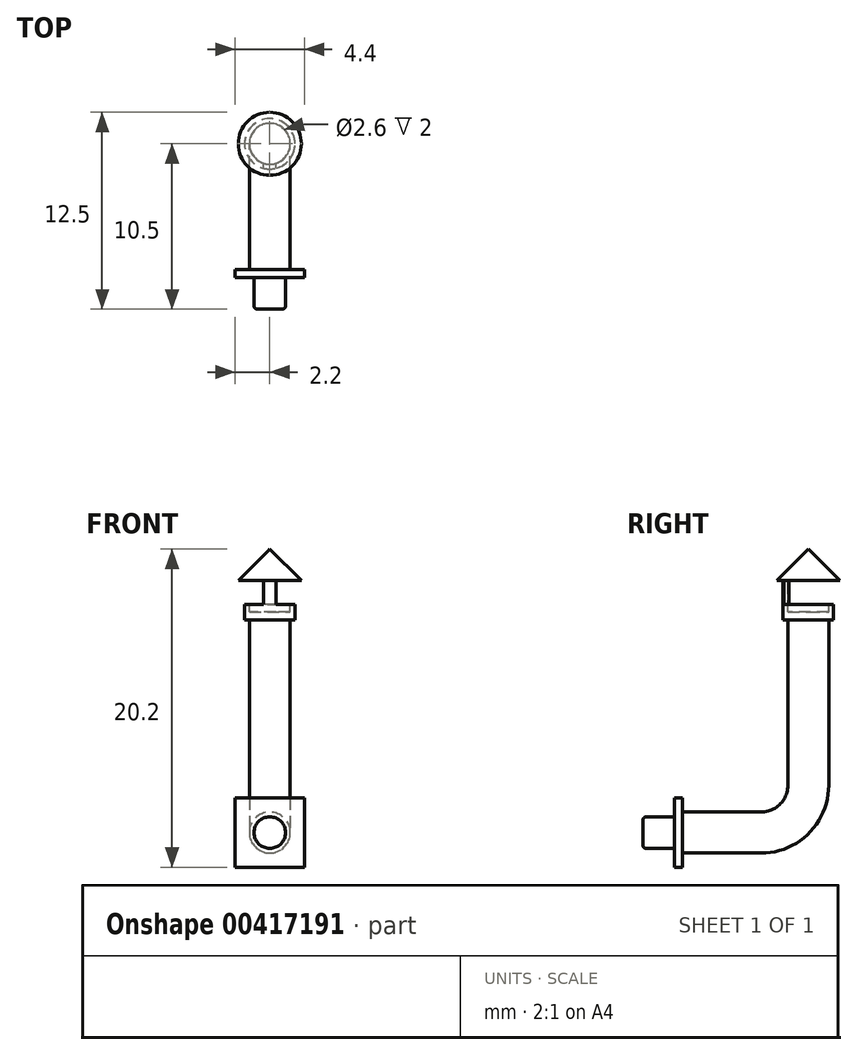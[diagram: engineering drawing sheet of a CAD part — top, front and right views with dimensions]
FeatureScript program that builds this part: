
annotation { "Feature Type Name" : "Feature", "Feature Type Description" : "" }
export const myFeature = defineFeature(function(context is Context, id is Id, definition is map)
    precondition{}
    {
        {
            var Q0;
            Q0=qCreatedBy(makeId("Right.planeOp"),FACE);
            var sketch = newSketch(context, id + "F0", { "sketchPlane" : qUnion([Q0])});
            skLineSegment(sketch, "E0", {"start": v(0, 0) * mm, "end": v(5, 0) * mm});
            skLineSegment(sketch, "E1", {"start": v(8, 3) * mm, "end": v(8, 14) * mm});
            skPoint(sketch, "E2.visualSharp", {"position": v(8, 0) * mm});
            skArc(sketch, "E2.filletArc", {"start": v(5, 0) * mm, "mid": v(7.12, 0.88) * mm, "end": v(8, 3) * mm});
            skSolve(sketch);
        }
        {
            var Q0;
            Q0=qCreatedBy(makeId("Front.planeOp"),FACE);
            var sketch = newSketch(context, id + "F1", { "sketchPlane" : qUnion([Q0])});
            skCircle(sketch, "E3", {"center": v(0, 0) * mm, "radius": 1.3 * mm});
            skSolve(sketch);
        }
        {
            var Q0;
            Q0=makeQuery(id+"F1.imprint","IMPRINT",FACE,{"disambiguationData":[TD([[makeQuery(id+"F1.imprint","IMPRINT",EDGE,{"derivedFrom":sQuery(id+"F1.wireOp",EDGE,"E3")}),1.0]])]});
            var Q1;
            Q1=sQuery(id+"F0.wireOp",EDGE,"E0");
            var Q2;
            Q2=sQuery(id+"F0.wireOp",EDGE,"E2.filletArc");
            var Q3;
            Q3=sQuery(id+"F0.wireOp",EDGE,"E1");
            sweep(context, id + "F2", {"profiles" : qUnion([Q0]), "path" : qUnion([Q1, Q2, Q3])});
        }
        {
            var Q0;
            Q0=makeQuery(id+"F2.opSweep","CAP_FACE",FACE,{"disambiguationData":[OSD([sQuery(id+"F0.wireOp",VERTEX,"E0.start"),sQuery(id+"F1.wireOp",EDGE,"E3")])],"isStart":true});
            var sketch = newSketch(context, id + "F3", { "sketchPlane" : qUnion([Q0])});
            skLineSegment(sketch, "E4.bottom", {"start": v(2.2, 2.2) * mm, "end": v(-2.2, 2.2) * mm});
            skLineSegment(sketch, "E4.top", {"start": v(2.2, -2.2) * mm, "end": v(-2.2, -2.2) * mm});
            skLineSegment(sketch, "E4.left", {"start": v(2.2, 2.2) * mm, "end": v(2.2, -2.2) * mm});
            skLineSegment(sketch, "E4.right", {"start": v(-2.2, 2.2) * mm, "end": v(-2.2, -2.2) * mm});
            skPoint(sketch, "E4.middle", {"position": v(0, 0) * mm});
            skSolve(sketch);
        }
        {
            var Q0;
            Q0=makeQuery(id+"F3.imprint","IMPRINT",FACE,{"disambiguationData":[TD([[makeQuery(id+"F3.imprint","IMPRINT",EDGE,{"derivedFrom":sQuery(id+"F3.wireOp",EDGE,"E4.bottom")}),1.0]])]});
            var Q1;
            Q1=makeQuery(id+"F3.imprint","IMPRINT",FACE,{"disambiguationData":[TD([[makeQuery(id+"F3.imprint","IMPRINT",EDGE,{"derivedFrom":makeQuery(id+"F2.opSweep","CAP_EDGE",EDGE,{"disambiguationData":[OSD([sQuery(id+"F0.wireOp",VERTEX,"E0.start"),sQuery(id+"F1.wireOp",EDGE,"E3")])],"isStart":true})}),-1.0]])]});
            extrude(context, id + "F4", {"entities" : qUnion([Q0, Q1]), "operationType" : NewBodyOperationType.ADD, "depth" : 0.5 * mm});
        }
        {
            var Q0;
            Q0=makeQuery(id+"F4.opExtrude","CAP_FACE",FACE,{"disambiguationData":[OSD([sQuery(id+"F3.wireOp",EDGE,"E4.bottom"),sQuery(id+"F3.wireOp",EDGE,"E4.top"),sQuery(id+"F3.wireOp",EDGE,"E4.left"),sQuery(id+"F3.wireOp",EDGE,"E4.right")])],"isStart":false});
            var sketch = newSketch(context, id + "F5", { "sketchPlane" : qUnion([Q0])});
            skCircle(sketch, "E5", {"center": v(0, 0) * mm, "radius": 1 * mm});
            skSolve(sketch);
        }
        {
            var Q0;
            Q0=makeQuery(id+"F5.imprint","IMPRINT",FACE,{"disambiguationData":[TD([[makeQuery(id+"F5.imprint","IMPRINT",EDGE,{"derivedFrom":sQuery(id+"F5.wireOp",EDGE,"E5")}),1.0]])]});
            extrude(context, id + "F6", {"entities" : qUnion([Q0]), "operationType" : NewBodyOperationType.ADD, "depth" : 2 * mm});
        }
        {
            var Q0;
            Q0=makeQuery(id+"F6.opExtrude","CAP_EDGE",EDGE,{"disambiguationData":[OSD([sQuery(id+"F5.wireOp",EDGE,"E5")])],"isStart":false});
            fillet(context, id + "F7", {"entities" : qUnion([Q0]), "radius" : 0.2 * mm, "tangentPropagation" : true, "allowEdgeOverflow" : false});
        }
        {
            var Q0;
            Q0=makeQuery(id+"F2.opSweep","CAP_FACE",FACE,{"disambiguationData":[OSD([sQuery(id+"F0.wireOp",VERTEX,"E1.end"),sQuery(id+"F1.wireOp",EDGE,"E3")])],"isStart":false});
            var sketch = newSketch(context, id + "F8", { "sketchPlane" : qUnion([Q0])});
            skCircle(sketch, "E6", {"center": v(0, 8) * mm, "radius": 1.6 * mm});
            skSolve(sketch);
        }
        {
            var Q0;
            Q0=makeQuery(id+"F8.imprint","IMPRINT",FACE,{"disambiguationData":[TD([[makeQuery(id+"F8.imprint","IMPRINT",EDGE,{"derivedFrom":sQuery(id+"F8.wireOp",EDGE,"E6")}),1.0]])]});
            extrude(context, id + "F9", {"entities" : qUnion([Q0]), "operationType" : NewBodyOperationType.ADD, "oppositeDirection" : true, "depth" : 0.5 * mm, "hasSecondDirection" : true, "secondDirectionOppositeDirection" : false, "secondDirectionDepth" : 0.5 * mm});
        }
        {
            var Q0;
            Q0=makeQuery(id+"F9.opExtrude","CAP_FACE",FACE,{"disambiguationData":[OSD([sQuery(id+"F0.wireOp",VERTEX,"E1.end"),sQuery(id+"F1.wireOp",EDGE,"E3"),sQuery(id+"F8.wireOp",EDGE,"E6")])],"isStart":true});
            var sketch = newSketch(context, id + "F10", { "sketchPlane" : qUnion([Q0])});
            skLineSegment(sketch, "E7", {"start": v(-0.4, 6.08) * mm, "end": v(-0.4, 7.19) * mm, "construction": true});
            skLineSegment(sketch, "E8", {"start": v(0.4, 6.11) * mm, "end": v(0.4, 7.36) * mm, "construction": true});
            skLineSegment(sketch, "E9", {"start": v(-0.4, 6.45) * mm, "end": v(-0.4, 6.76) * mm});
            skLineSegment(sketch, "E10", {"start": v(0.4, 6.45) * mm, "end": v(0.4, 6.76) * mm});
            skLineSegment(sketch, "E11", {"start": v(0, 6.08) * mm, "end": v(0, 7.03) * mm, "construction": true});
            skCircle(sketch, "E12.0", {"center": v(0, 8) * mm, "radius": 1.6 * mm});
            skCircle(sketch, "E13.0", {"center": v(0, 8) * mm, "radius": 1.3 * mm});
            skArc(sketch, "E14", {"start": v(-0.4, 6.45) * mm, "mid": v(0, 6.4) * mm, "end": v(0.4, 6.45) * mm});
            skArc(sketch, "E15", {"start": v(-0.4, 6.76) * mm, "mid": v(0, 6.7) * mm, "end": v(0.4, 6.76) * mm});
            skSolve(sketch);
        }
        {
            var Q0;
            {var subQ0=sQuery(id+"F10.wireOp",EDGE,"E9");Q0=makeQuery(id+"F10.imprint","IMPRINT",FACE,{"disambiguationData":[TD([[makeQuery(id+"F10.imprint","IMPRINT",EDGE,{"derivedFrom":subQ0}),-1.0]])]});}
            extrude(context, id + "F11", {"entities" : qUnion([Q0]), "operationType" : NewBodyOperationType.ADD, "depth" : 1.5 * mm});
        }
        {
            var Q0;
            Q0=qCreatedBy(makeId("Right.planeOp"),FACE);
            var sketch = newSketch(context, id + "F12", { "sketchPlane" : qUnion([Q0])});
            skLineSegment(sketch, "E16", {"start": v(8, 17.4) * mm, "end": v(8, 9.63) * mm, "construction": true});
            skLineSegment(sketch, "E17", {"start": v(6.7, 3) * mm, "end": v(6.7, 13.5) * mm});
            skLineSegment(sketch, "E18", {"start": v(9.3, 13.5) * mm, "end": v(9.3, 3) * mm});
            skSolve(sketch);
        }
        {
            var Q0;
            Q0=qCreatedBy(makeId("Right.planeOp"),FACE);
            var sketch = newSketch(context, id + "F13", { "sketchPlane" : qUnion([Q0])});
            skLineSegment(sketch, "E19", {"start": v(6.7, 3) * mm, "end": v(6.7, 13.5) * mm});
            skLineSegment(sketch, "E20", {"start": v(9.3, 13.5) * mm, "end": v(9.3, 3) * mm});
            skLineSegment(sketch, "E21", {"start": v(8, 12.52) * mm, "end": v(8, 23.32) * mm, "construction": true});
            skLineSegment(sketch, "E22.0", {"start": v(6.45, 16) * mm, "end": v(6.76, 16) * mm});
            skLineSegment(sketch, "E23", {"start": v(8, 16) * mm, "end": v(6, 16) * mm});
            skLineSegment(sketch, "E24", {"start": v(8, 16) * mm, "end": v(8, 18) * mm});
            skLineSegment(sketch, "E25", {"start": v(8, 18) * mm, "end": v(6, 16) * mm});
            skSolve(sketch);
        }
        {
            var Q0;
            {var subQ0=sQuery(id+"F13.wireOp",EDGE,"E24");Q0=makeQuery(id+"F13.imprint","IMPRINT",FACE,{"disambiguationData":[TD([[makeQuery(id+"F13.imprint","IMPRINT",EDGE,{"derivedFrom":subQ0}),1.0]])]});}
            var Q1;
            Q1=sQuery(id+"F13.wireOp",EDGE,"E21");
            revolve(context, id + "F14", {"operationType" : NewBodyOperationType.ADD, "entities" : qUnion([Q0]), "axis" : qUnion([Q1]), "revolveType" : RevolveType.FULL});
        }
    });
